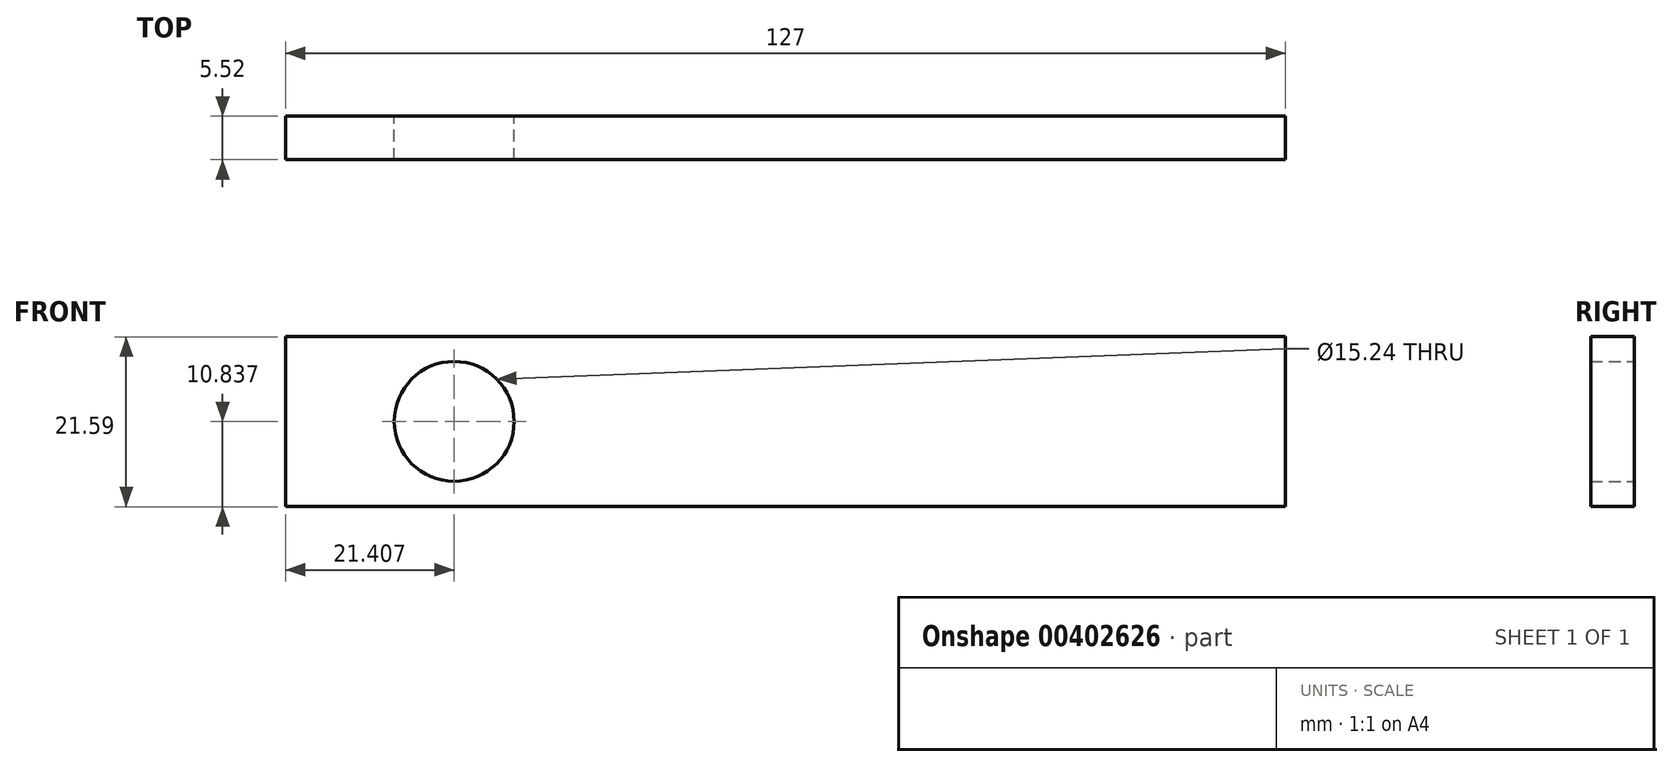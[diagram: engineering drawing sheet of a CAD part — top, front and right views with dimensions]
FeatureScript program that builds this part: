
annotation { "Feature Type Name" : "Feature", "Feature Type Description" : "" }
export const myFeature = defineFeature(function(context is Context, id is Id, definition is map)
    precondition{}
    {
        {
            var Q0;
            Q0=qCreatedBy(makeId("Front.planeOp"),FACE);
            var sketch = newSketch(context, id + "F0", { "sketchPlane" : qUnion([Q0])});
            skLineSegment(sketch, "E0.bottom", {"start": v(-48.8, 22.22) * mm, "end": v(78.2, 22.22) * mm});
            skLineSegment(sketch, "E0.top", {"start": v(-48.8, 0.63) * mm, "end": v(78.2, 0.63) * mm});
            skLineSegment(sketch, "E0.left", {"start": v(-48.8, 22.22) * mm, "end": v(-48.8, 0.63) * mm});
            skLineSegment(sketch, "E0.right", {"start": v(78.2, 22.22) * mm, "end": v(78.2, 0.63) * mm});
            skPoint(sketch, "E0.middle", {"position": v(14.7, 11.43) * mm});
            skCircle(sketch, "E1", {"center": v(-27.4, 11.47) * mm, "radius": 7.62 * mm});
            skSolve(sketch);
        }
        {
            var Q0;
            Q0 = qSketchRegion(id + "F0", true);
            extrude(context, id + "F1", {"entities" : qUnion([Q0]), "depth" : 5.52 * mm});
        }
        {
            var Q0;
            Q0=qCreatedBy(makeId("Front.planeOp"),FACE);
            var sketch = newSketch(context, id + "F2", { "sketchPlane" : qUnion([Q0])});
            skText(sketch, "E2", { "text": "bazmarc", "fontName": "Tinos-Regular.ttf"});
            const initialGuessF2  = {"E2": [0.01253, 0.00966, 1, 0, 0.00847]};
            skSetInitialGuess(sketch, initialGuessF2);
            skSolve(sketch);
        }
        {
            var Q0;
            Q0 = qBodyType(qCreatedBy(id + "F2" ,EDGE), BodyType.WIRE);
            extrude(context, id + "F3", {"bodyType" : ToolBodyType.SURFACE, "surfaceEntities" : qUnion([Q0]), "endBound" : BoundingType.SYMMETRIC, "depth" : 25.4 * mm});
        }
    });
